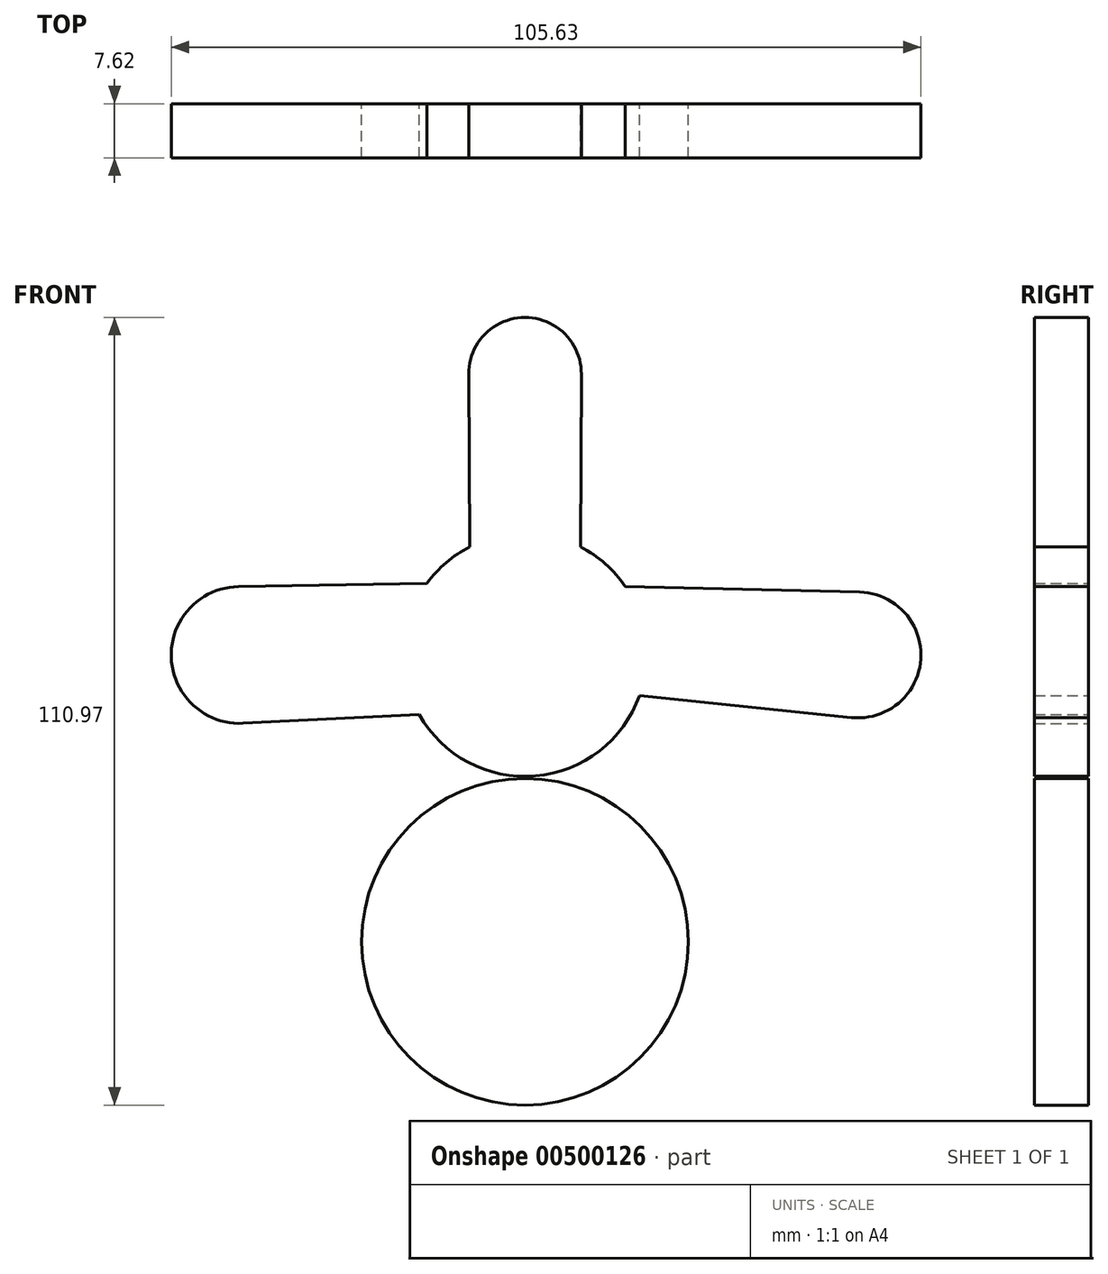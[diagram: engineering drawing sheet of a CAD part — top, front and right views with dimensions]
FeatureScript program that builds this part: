
annotation { "Feature Type Name" : "Feature", "Feature Type Description" : "" }
export const myFeature = defineFeature(function(context is Context, id is Id, definition is map)
    precondition{}
    {
        {
            var Q0;
            Q0=qCreatedBy(makeId("Front.planeOp"),FACE);
            var sketch = newSketch(context, id + "F0", { "sketchPlane" : qUnion([Q0])});
            skCircle(sketch, "E0", {"center": v(0, 0) * mm, "radius": 17.11 * mm});
            skCircle(sketch, "E1", {"center": v(46.94, 0) * mm, "radius": 8.86 * mm});
            skCircle(sketch, "E2", {"center": v(0, 39.6) * mm, "radius": 7.94 * mm});
            skCircle(sketch, "E3", {"center": v(-40.2, 0) * mm, "radius": 9.64 * mm});
            skCircle(sketch, "E4", {"center": v(0, -40.4) * mm, "radius": 23.01 * mm});
            skLineSegment(sketch, "E5", {"start": v(-14.92, -8.37) * mm, "end": v(-39.72, -9.62) * mm});
            skLineSegment(sketch, "E6", {"start": v(-13.8, 10.1) * mm, "end": v(-40.37, 9.64) * mm});
            skLineSegment(sketch, "E7", {"start": v(-7.81, 15.22) * mm, "end": v(-7.94, 39.57) * mm});
            skLineSegment(sketch, "E8", {"start": v(7.81, 15.22) * mm, "end": v(7.94, 39.57) * mm});
            skLineSegment(sketch, "E9", {"start": v(14.14, 9.64) * mm, "end": v(47.15, 8.85) * mm});
            skLineSegment(sketch, "E10", {"start": v(16.13, -5.7) * mm, "end": v(47.15, -8.93) * mm});
            skSolve(sketch);
        }
        {
            var Q0;
            Q0 = qSketchRegion(id + "F0", true);
            extrude(context, id + "F1", {"entities" : qUnion([Q0]), "depth" : 7.62 * mm});
        }
    });
